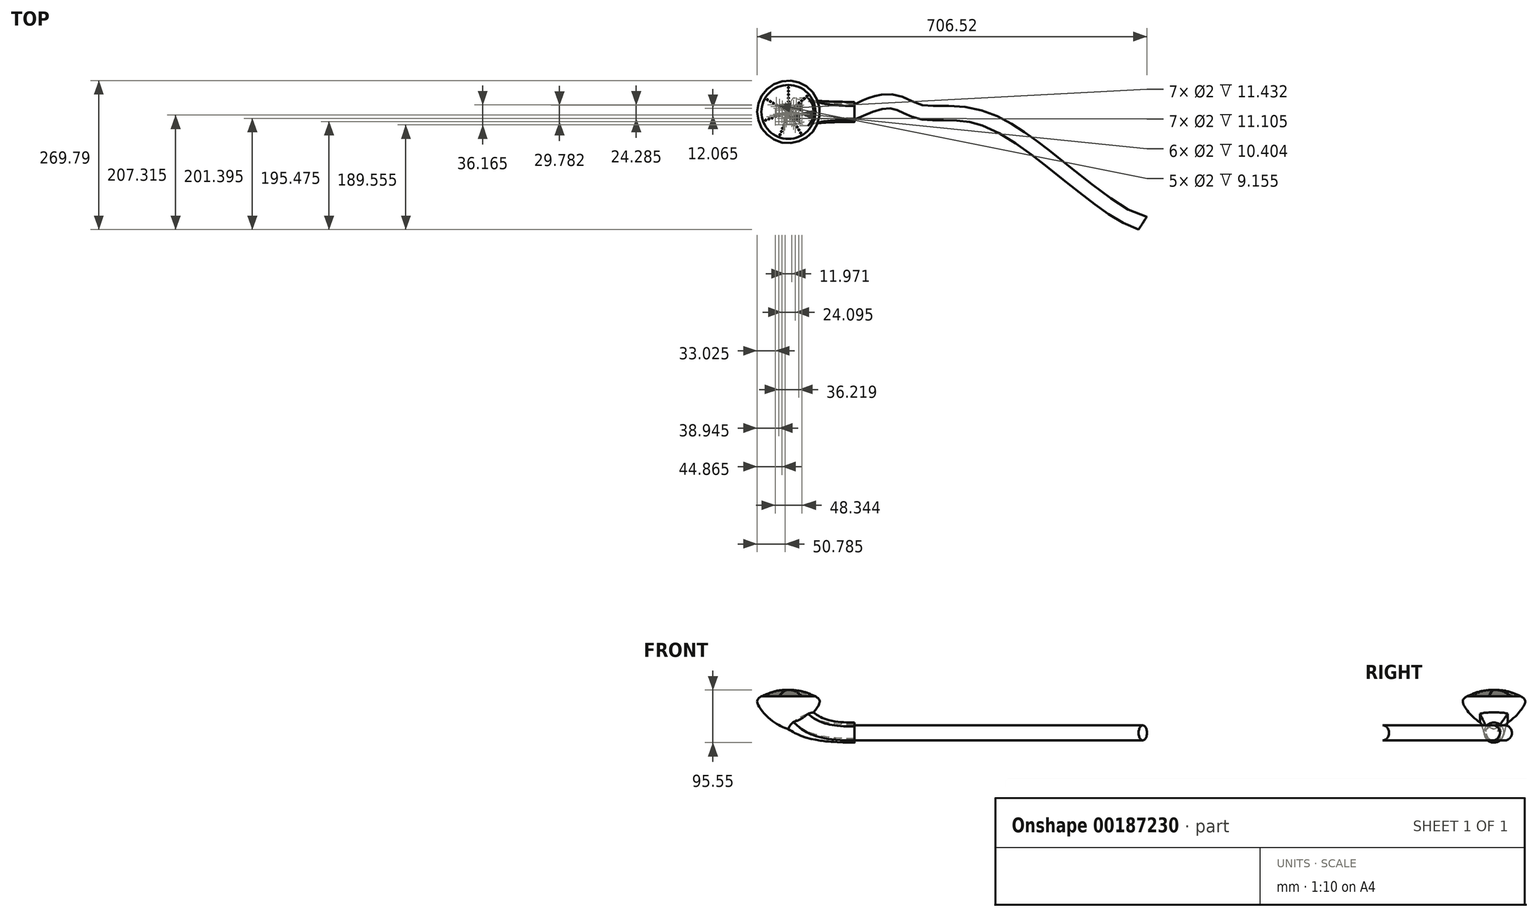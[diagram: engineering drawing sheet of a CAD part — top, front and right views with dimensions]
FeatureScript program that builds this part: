
annotation { "Feature Type Name" : "Feature", "Feature Type Description" : "" }
export const myFeature = defineFeature(function(context is Context, id is Id, definition is map)
    precondition{}
    {
        {
            var Q0;
            Q0=qCreatedBy(makeId("Front.planeOp"),FACE);
            var sketch = newSketch(context, id + "F0", { "sketchPlane" : qUnion([Q0])});
            skFitSpline(sketch, "E0", {"points": [v(0, 11.56) * mm, v(-22.4, 9.56) * mm, v(-48.98, 0) * mm], "startDerivative": vector(-46.84, -0.99) * mm, "endDerivative": vector(-51.04, -21.74) * mm});
            skFitSpline(sketch, "E1", {"points": [v(-48.98, 0) * mm, v(-56.63, -9.38) * mm, v(-30.59, -43.6) * mm, v(0, -59.63) * mm], "startDerivative": vector(-52.62, -33.3) * mm, "endDerivative": vector(79.63, -29.74) * mm});
            skLineSegment(sketch, "E2", {"start": v(0, 11.56) * mm, "end": v(0, -59.63) * mm});
            skSolve(sketch);
        }
        {
            var Q0;
            Q0 = qSketchRegion(id + "F0", true);
            var Q1;
            Q1=sQuery(id+"F0.wireOp",EDGE,"E2");
            revolve(context, id + "F1", {"entities" : qUnion([Q0]), "axis" : qUnion([Q1]), "revolveType" : RevolveType.FULL});
        }
        {
            var Q0;
            Q0=qCreatedBy(makeId("Front.planeOp"),FACE);
            var sketch = newSketch(context, id + "F2", { "sketchPlane" : qUnion([Q0])});
            skFitSpline(sketch, "E3", {"points": [v(49.7, -29.4) * mm, v(44.43, -29.4) * mm, v(16.02, -41.24) * mm, v(2.56, -73.18) * mm], "startDerivative": vector(-26.45, 3.2) * mm, "endDerivative": vector(59.28, -95.66) * mm});
            skLineSegment(sketch, "E4", {"start": v(2.56, -73.18) * mm, "end": v(49.7, -29.4) * mm});
            skSolve(sketch);
        }
        {
            var Q0;
            Q0 = qSketchRegion(id + "F2", true);
            extrude(context, id + "F3", {"entities" : qUnion([Q0]), "operationType" : NewBodyOperationType.REMOVE, "oppositeDirection" : true, "depth" : 25 * mm, "hasSecondDirection" : true, "secondDirectionOppositeDirection" : false, "secondDirectionDepth" : 25 * mm});
        }
        {
            var Q0;
            Q0=qCreatedBy(makeId("Right.planeOp"),FACE);
            cPlane(context, id + "F4", {"entities" : qUnion([Q0]), "cplaneType" : CPlaneType.OFFSET, "offset" : 120 * mm, "width" : 150 * mm, "height" : 150 * mm});
        }
        {
            var Q0;
            Q0=qCreatedBy(id+"F4.planeOp",FACE);
            var sketch = newSketch(context, id + "F5", { "sketchPlane" : qUnion([Q0])});
            skCircle(sketch, "E5", {"center": v(0, -65.86) * mm, "radius": 18.13 * mm});
            skSolve(sketch);
        }
        {
            var Q1;
            Q1=makeQuery(id+"F5.imprint","IMPRINT",FACE,{"disambiguationData":[TD([[makeQuery(id+"F5.imprint","IMPRINT",EDGE,{"derivedFrom":sQuery(id+"F5.wireOp",EDGE,"E5")}),1.0]])]});
            var Q2;
            Q2=makeQuery(id+"F3.boolean.opBoolean","COPY",FACE,{"derivedFrom":makeQuery(id+"F3.opExtrude","SWEPT_FACE",FACE,{"disambiguationData":[OSD([sQuery(id+"F2.wireOp",EDGE,"E3")])]})});
            loft(context, id + "F6", {"operationType" : NewBodyOperationType.ADD, "startCondition" : LoftEndDerivativeType.NORMAL_TO_PROFILE, "startMagnitude" : 2, "sheetProfilesArray" : [{ "sheetProfileEntities" : qUnion([Q1]) }, { "sheetProfileEntities" : qUnion([Q2]) }]});
        }
        {
            var Q0;
            Q0=makeQuery(id+"F6.opLoft","CAP_FACE",FACE,{"disambiguationData":[OSD([makeQuery(id+"F5.imprint","IMPRINT",FACE,{"disambiguationData":[TD([[makeQuery(id+"F5.imprint","IMPRINT",EDGE,{"derivedFrom":sQuery(id+"F5.wireOp",EDGE,"E5")}),1.0]])]})])],"isStart":true});
            var sketch = newSketch(context, id + "F7", { "sketchPlane" : qUnion([Q0])});
            skCircle(sketch, "E6", {"center": v(0, -66.32) * mm, "radius": 13.77 * mm});
            skSolve(sketch);
        }
        {
            var Q0;
            Q0=qCreatedBy(makeId("Top.planeOp"),FACE);
            cPlane(context, id + "F8", {"entities" : qUnion([Q0]), "cplaneType" : CPlaneType.OFFSET, "offset" : 65 * mm, "oppositeDirection" : true, "width" : 150 * mm, "height" : 150 * mm});
        }
        {
            var Q0;
            Q0=qCreatedBy(id+"F8.planeOp",FACE);
            var sketch = newSketch(context, id + "F9", { "sketchPlane" : qUnion([Q0])});
            skFitSpline(sketch, "E7", {"points": [v(120.28, 0) * mm, v(179.2, 19.33) * mm, v(239.75, 0) * mm, v(366.67, -16.8) * mm, v(642.61, -201.77) * mm], "startDerivative": vector(153.64, 57.65) * mm, "endDerivative": vector(500.26, -110.98) * mm});
            skSolve(sketch);
        }
        {
            var Q0;
            Q0 = qSketchRegion(id + "F7", true);
            var Q1;
            Q1=sQuery(id+"F9.wireOp",EDGE,"E7");
            sweep(context, id + "F10", {"operationType" : NewBodyOperationType.ADD, "profiles" : qUnion([Q0]), "path" : qUnion([Q1])});
        }
        {
            var Q0;
            Q0=qCreatedBy(makeId("Top.planeOp"),FACE);
            var sketch = newSketch(context, id + "F11", { "sketchPlane" : qUnion([Q0])});
            skCircle(sketch, "E8", {"center": v(0, 6.22) * mm, "radius": 1 * mm});
            skCircle(sketch, "E9.0.1.0", {"center": v(0, 12.52) * mm, "radius": 1 * mm});
            skCircle(sketch, "E9.0.2.0", {"center": v(0, 18.82) * mm, "radius": 1 * mm});
            skCircle(sketch, "E9.0.3.0", {"center": v(0, 25.12) * mm, "radius": 1 * mm});
            skCircle(sketch, "E9.0.4.0", {"center": v(0, 31.42) * mm, "radius": 1 * mm});
            skCircle(sketch, "E9.0.5.0", {"center": v(0, 37.72) * mm, "radius": 1 * mm});
            skCircle(sketch, "E9.0.6.0", {"center": v(0, 44.02) * mm, "radius": 1 * mm});
            skLineSegment(sketch, "E9.direction1", {"start": v(0, 6.22) * mm, "end": v(20.2, 6.22) * mm, "construction": true});
            skLineSegment(sketch, "E9.direction2", {"start": v(0, 6.22) * mm, "end": v(0, 12.52) * mm, "construction": true});
            skCircle(sketch, "E10.1.0", {"center": v(4.76, 4) * mm, "radius": 1 * mm});
            skCircle(sketch, "E10.1.1", {"center": v(9.6, 8.05) * mm, "radius": 1 * mm});
            skCircle(sketch, "E10.1.2", {"center": v(14.42, 12.1) * mm, "radius": 1 * mm});
            skCircle(sketch, "E10.1.3", {"center": v(19.24, 16.15) * mm, "radius": 1 * mm});
            skCircle(sketch, "E10.1.4", {"center": v(24.07, 20.2) * mm, "radius": 1 * mm});
            skCircle(sketch, "E10.1.5", {"center": v(28.9, 24.25) * mm, "radius": 1 * mm});
            skCircle(sketch, "E10.1.6", {"center": v(33.72, 28.3) * mm, "radius": 1 * mm});
            skLineSegment(sketch, "E10.1.7", {"start": v(4.76, 4) * mm, "end": v(9.6, 8.05) * mm, "construction": true});
            skCircle(sketch, "E10.2.0", {"center": v(6.13, -1.08) * mm, "radius": 1 * mm});
            skCircle(sketch, "E10.2.1", {"center": v(12.33, -2.17) * mm, "radius": 1 * mm});
            skCircle(sketch, "E10.2.2", {"center": v(18.53, -3.27) * mm, "radius": 1 * mm});
            skCircle(sketch, "E10.2.3", {"center": v(24.74, -4.36) * mm, "radius": 1 * mm});
            skCircle(sketch, "E10.2.4", {"center": v(30.94, -5.46) * mm, "radius": 1 * mm});
            skCircle(sketch, "E10.2.5", {"center": v(37.15, -6.55) * mm, "radius": 1 * mm});
            skCircle(sketch, "E10.2.6", {"center": v(43.35, -7.64) * mm, "radius": 1 * mm});
            skLineSegment(sketch, "E10.2.7", {"start": v(6.13, -1.08) * mm, "end": v(12.33, -2.17) * mm, "construction": true});
            skPoint(sketch, "E10.center", {"position": v(0, 0) * mm});
            skLineSegment(sketch, "E10.anchor1", {"start": v(0, 0) * mm, "end": v(0, 6.22) * mm, "construction": true});
            skLineSegment(sketch, "E10.anchor2", {"start": v(0, 0) * mm, "end": v(-5.39, 3.11) * mm, "construction": true});
            skCircle(sketch, "E11.1.3.0", {"center": v(3.11, -5.39) * mm, "radius": 1 * mm});
            skCircle(sketch, "E11.2.3.0", {"center": v(6.26, -10.84) * mm, "radius": 1 * mm});
            skCircle(sketch, "E11.4.3.0", {"center": v(9.41, -16.3) * mm, "radius": 1 * mm});
            skCircle(sketch, "E11.6.3.0", {"center": v(12.56, -21.75) * mm, "radius": 1 * mm});
            skCircle(sketch, "E11.8.3.0", {"center": v(15.71, -27.21) * mm, "radius": 1 * mm});
            skCircle(sketch, "E11.10.3.0", {"center": v(18.86, -32.67) * mm, "radius": 1 * mm});
            skCircle(sketch, "E11.12.3.0", {"center": v(22.01, -38.12) * mm, "radius": 1 * mm});
            skLineSegment(sketch, "E11.14.3.0", {"start": v(3.11, -5.39) * mm, "end": v(6.26, -10.84) * mm, "construction": true});
            skCircle(sketch, "E12.1.4.0", {"center": v(-2.13, -5.84) * mm, "radius": 1 * mm});
            skCircle(sketch, "E12.2.4.0", {"center": v(-4.28, -11.77) * mm, "radius": 1 * mm});
            skCircle(sketch, "E12.4.4.0", {"center": v(-6.44, -17.69) * mm, "radius": 1 * mm});
            skCircle(sketch, "E12.6.4.0", {"center": v(-8.6, -23.6) * mm, "radius": 1 * mm});
            skCircle(sketch, "E12.8.4.0", {"center": v(-10.75, -29.53) * mm, "radius": 1 * mm});
            skCircle(sketch, "E12.10.4.0", {"center": v(-12.9, -35.45) * mm, "radius": 1 * mm});
            skCircle(sketch, "E12.12.4.0", {"center": v(-15.06, -41.37) * mm, "radius": 1 * mm});
            skLineSegment(sketch, "E12.14.4.0", {"start": v(-2.13, -5.84) * mm, "end": v(-4.28, -11.77) * mm, "construction": true});
            skCircle(sketch, "E12.1.5.0", {"center": v(-5.84, -2.13) * mm, "radius": 1 * mm});
            skCircle(sketch, "E12.2.5.0", {"center": v(-11.77, -4.28) * mm, "radius": 1 * mm});
            skCircle(sketch, "E12.4.5.0", {"center": v(-17.69, -6.44) * mm, "radius": 1 * mm});
            skCircle(sketch, "E12.6.5.0", {"center": v(-23.6, -8.6) * mm, "radius": 1 * mm});
            skCircle(sketch, "E12.8.5.0", {"center": v(-29.53, -10.75) * mm, "radius": 1 * mm});
            skCircle(sketch, "E12.10.5.0", {"center": v(-35.45, -12.9) * mm, "radius": 1 * mm});
            skCircle(sketch, "E12.12.5.0", {"center": v(-41.37, -15.06) * mm, "radius": 1 * mm});
            skLineSegment(sketch, "E12.14.5.0", {"start": v(-5.84, -2.13) * mm, "end": v(-11.77, -4.28) * mm, "construction": true});
            skCircle(sketch, "E12.1.6.0", {"center": v(-5.39, 3.11) * mm, "radius": 1 * mm});
            skCircle(sketch, "E12.2.6.0", {"center": v(-10.84, 6.26) * mm, "radius": 1 * mm});
            skCircle(sketch, "E12.4.6.0", {"center": v(-16.3, 9.41) * mm, "radius": 1 * mm});
            skCircle(sketch, "E12.6.6.0", {"center": v(-21.75, 12.56) * mm, "radius": 1 * mm});
            skCircle(sketch, "E12.8.6.0", {"center": v(-27.21, 15.71) * mm, "radius": 1 * mm});
            skCircle(sketch, "E12.10.6.0", {"center": v(-32.67, 18.86) * mm, "radius": 1 * mm});
            skCircle(sketch, "E12.12.6.0", {"center": v(-38.12, 22.01) * mm, "radius": 1 * mm});
            skLineSegment(sketch, "E12.14.6.0", {"start": v(-5.39, 3.11) * mm, "end": v(-10.84, 6.26) * mm, "construction": true});
            skSolve(sketch);
        }
        {
            var Q0;
            Q0 = qSketchRegion(id + "F11", true);
            extrude(context, id + "F12", {"entities" : qUnion([Q0]), "operationType" : NewBodyOperationType.REMOVE, "depth" : 27.2 * mm});
        }
    });
